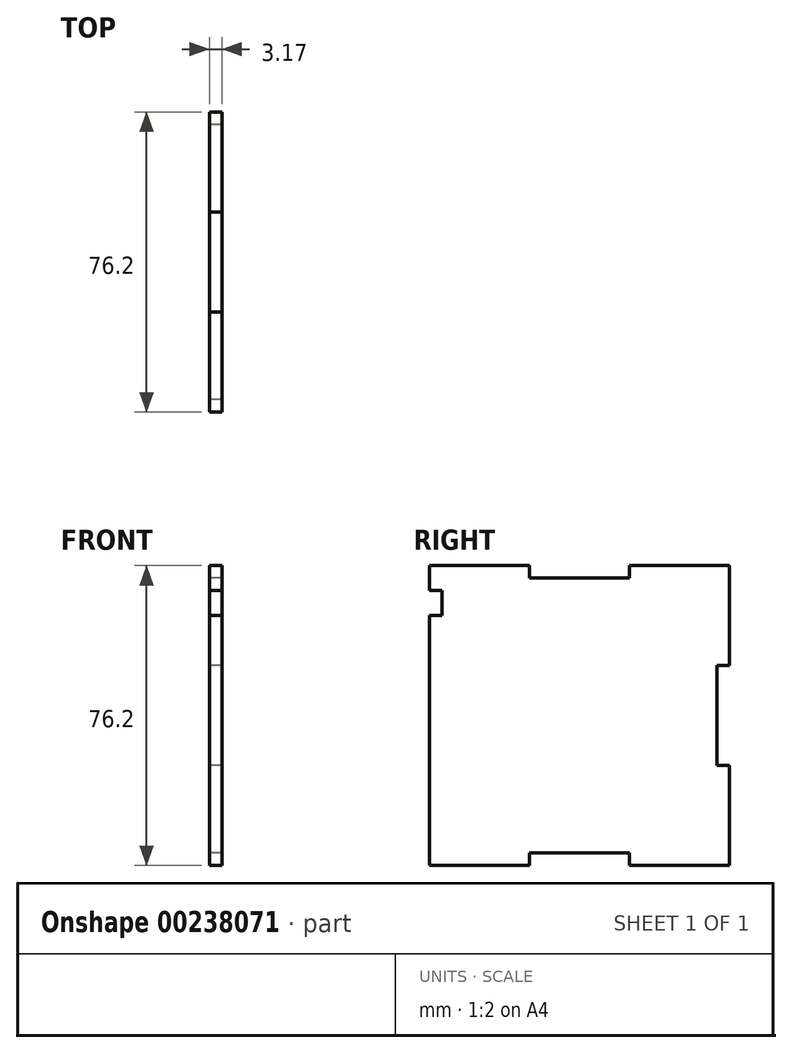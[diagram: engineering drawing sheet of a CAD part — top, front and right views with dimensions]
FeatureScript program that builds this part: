
annotation { "Feature Type Name" : "Feature", "Feature Type Description" : "" }
export const myFeature = defineFeature(function(context is Context, id is Id, definition is map)
    precondition{}
    {
        {
            var Q0;
            Q0=qCreatedBy(makeId("Right.planeOp"),FACE);
            var sketch = newSketch(context, id + "F0", { "sketchPlane" : qUnion([Q0])});
            skLineSegment(sketch, "E0.bottom", {"start": v(38.1, -38.1) * mm, "end": v(-38.1, -38.1) * mm});
            skLineSegment(sketch, "E0.top", {"start": v(38.1, 38.1) * mm, "end": v(-38.1, 38.1) * mm});
            skLineSegment(sketch, "E0.left", {"start": v(38.1, -38.1) * mm, "end": v(38.1, 38.1) * mm});
            skLineSegment(sketch, "E0.right", {"start": v(-38.1, -38.1) * mm, "end": v(-38.1, 38.1) * mm});
            skPoint(sketch, "E0.middle", {"position": v(0, 0) * mm});
            skLineSegment(sketch, "E1.bottom", {"start": v(34.93, 12.7) * mm, "end": v(38.1, 12.7) * mm});
            skLineSegment(sketch, "E1.top", {"start": v(34.93, -12.7) * mm, "end": v(38.1, -12.7) * mm});
            skLineSegment(sketch, "E1.left", {"start": v(34.93, 12.7) * mm, "end": v(34.93, -12.7) * mm});
            skLineSegment(sketch, "E1.right", {"start": v(38.1, 12.7) * mm, "end": v(38.1, -12.7) * mm});
            skLineSegment(sketch, "E2.bottom", {"start": v(-12.7, 38.1) * mm, "end": v(12.7, 38.1) * mm});
            skLineSegment(sketch, "E2.top", {"start": v(-12.7, 34.92) * mm, "end": v(12.7, 34.92) * mm});
            skLineSegment(sketch, "E2.left", {"start": v(-12.7, 38.1) * mm, "end": v(-12.7, 34.92) * mm});
            skLineSegment(sketch, "E2.right", {"start": v(12.7, 38.1) * mm, "end": v(12.7, 34.92) * mm});
            skLineSegment(sketch, "E3.bottom", {"start": v(-12.7, -34.93) * mm, "end": v(12.7, -34.93) * mm});
            skLineSegment(sketch, "E3.top", {"start": v(-12.7, -38.1) * mm, "end": v(12.7, -38.1) * mm});
            skLineSegment(sketch, "E3.left", {"start": v(-12.7, -34.93) * mm, "end": v(-12.7, -38.1) * mm});
            skLineSegment(sketch, "E3.right", {"start": v(12.7, -34.93) * mm, "end": v(12.7, -38.1) * mm});
            skLineSegment(sketch, "E4.bottom", {"start": v(-38.1, 31.75) * mm, "end": v(-34.93, 31.75) * mm});
            skLineSegment(sketch, "E4.top", {"start": v(-38.1, 25.4) * mm, "end": v(-34.93, 25.4) * mm});
            skLineSegment(sketch, "E4.left", {"start": v(-38.1, 31.75) * mm, "end": v(-38.1, 25.4) * mm});
            skLineSegment(sketch, "E4.right", {"start": v(-34.93, 31.75) * mm, "end": v(-34.93, 25.4) * mm});
            skSolve(sketch);
        }
        {
            var Q0;
            {var subQ14=sQuery(id+"F0.wireOp",EDGE,"E1.bottom");Q0=makeQuery(id+"F0.imprint","IMPRINT",FACE,{"disambiguationData":[TD([[makeQuery(id+"F0.imprint","IMPRINT",EDGE,{"derivedFrom":subQ14}),1.0]])]});}
            extrude(context, id + "F1", {"entities" : qUnion([Q0]), "depth" : 3.17 * mm});
        }
    });
